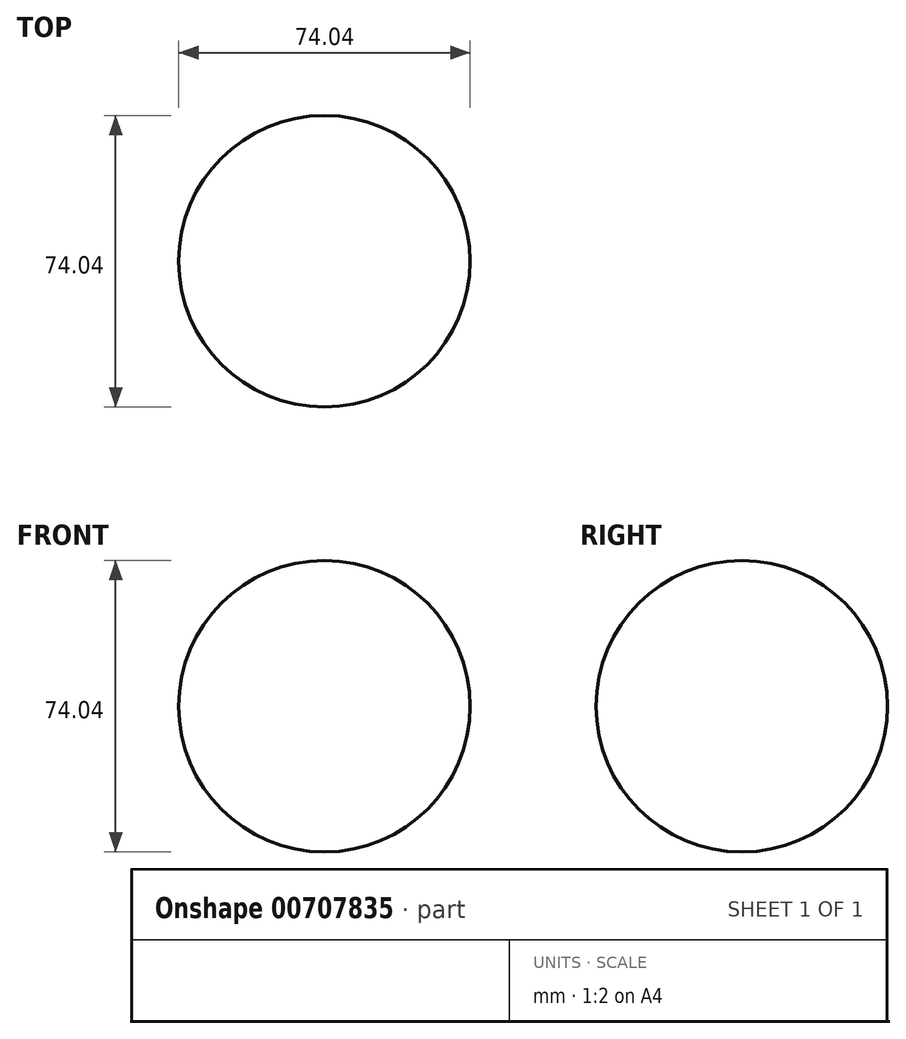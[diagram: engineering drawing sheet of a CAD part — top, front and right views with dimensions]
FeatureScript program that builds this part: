
annotation { "Feature Type Name" : "Feature", "Feature Type Description" : "" }
export const myFeature = defineFeature(function(context is Context, id is Id, definition is map)
    precondition{}
    {
        {
            var Q0;
            Q0=qCreatedBy(makeId("Front.planeOp"),FACE);
            var sketch = newSketch(context, id + "F0", { "sketchPlane" : qUnion([Q0])});
            skArc(sketch, "E0", {"start": v(0, -37.02) * mm, "mid": v(37.02, 0) * mm, "end": v(0, 37.02) * mm});
            skLineSegment(sketch, "E1", {"start": v(0, 37.02) * mm, "end": v(0, -37.02) * mm});
            skSolve(sketch);
        }
        {
            var Q0;
            Q0=makeQuery(id+"F0.imprint","IMPRINT",FACE,{"disambiguationData":[TD([[makeQuery(id+"F0.imprint","IMPRINT",EDGE,{"derivedFrom":sQuery(id+"F0.wireOp",EDGE,"E0")}),1.0]])]});
            var Q1;
            Q1=sQuery(id+"F0.wireOp",EDGE,"E1");
            revolve(context, id + "F1", {"surfaceOperationType" : NewSurfaceOperationType.NEW, "entities" : qUnion([Q0]), "axis" : qUnion([Q1]), "revolveType" : RevolveType.FULL});
        }
    });
